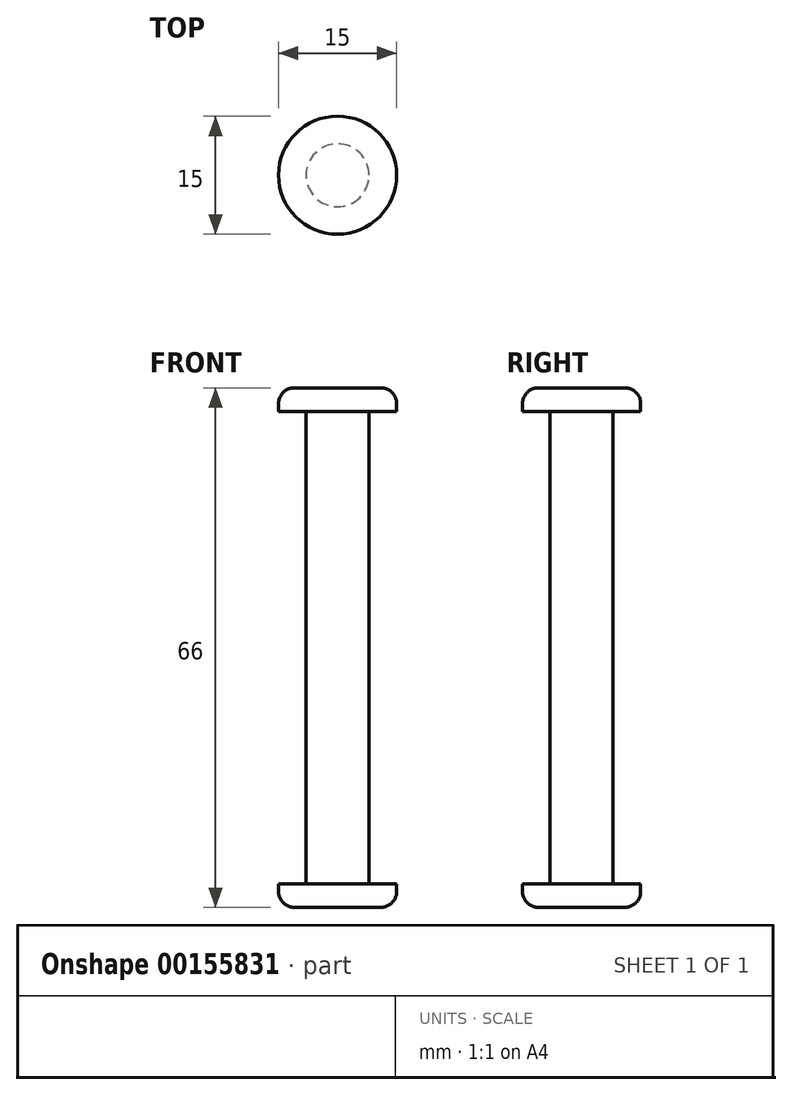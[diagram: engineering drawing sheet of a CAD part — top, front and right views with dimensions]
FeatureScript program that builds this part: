
annotation { "Feature Type Name" : "Feature", "Feature Type Description" : "" }
export const myFeature = defineFeature(function(context is Context, id is Id, definition is map)
    precondition{}
    {
        {
            var Q0;
            Q0=qCreatedBy(makeId("Top.planeOp"),FACE);
            var sketch = newSketch(context, id + "F0", { "sketchPlane" : qUnion([Q0])});
            skCircle(sketch, "E0", {"center": v(0, 0) * mm, "radius": 7.5 * mm});
            skSolve(sketch);
        }
        {
            var Q0;
            Q0 = qSketchRegion(id + "F0", true);
            extrude(context, id + "F1", {"entities" : qUnion([Q0]), "depth" : 3 * mm});
        }
        {
            var Q0;
            Q0=makeQuery(id+"F1.opExtrude","CAP_FACE",FACE,{"disambiguationData":[OSD([sQuery(id+"F0.wireOp",EDGE,"E0")])],"isStart":false});
            var sketch = newSketch(context, id + "F2", { "sketchPlane" : qUnion([Q0])});
            skCircle(sketch, "E1", {"center": v(0, 0) * mm, "radius": 4 * mm});
            skSolve(sketch);
        }
        {
            var Q0;
            Q0 = qSketchRegion(id + "F2", true);
            extrude(context, id + "F3", {"entities" : qUnion([Q0]), "operationType" : NewBodyOperationType.ADD, "depth" : 60 * mm});
        }
        {
            var Q0;
            Q0=makeQuery(id+"F3.opExtrude","CAP_FACE",FACE,{"disambiguationData":[OSD([sQuery(id+"F2.wireOp",EDGE,"E1")])],"isStart":false});
            var sketch = newSketch(context, id + "F4", { "sketchPlane" : qUnion([Q0])});
            skCircle(sketch, "E2", {"center": v(0, 0) * mm, "radius": 7.5 * mm});
            skSolve(sketch);
        }
        {
            var Q0;
            Q0 = qSketchRegion(id + "F4", true);
            extrude(context, id + "F5", {"entities" : qUnion([Q0]), "operationType" : NewBodyOperationType.ADD, "depth" : 3 * mm});
        }
        {
            var Q0;
            Q0=makeQuery(id+"F5.opExtrude","CAP_EDGE",EDGE,{"disambiguationData":[OSD([sQuery(id+"F4.wireOp",EDGE,"E2")])],"isStart":false});
            var Q1;
            Q1=makeQuery(id+"F1.opExtrude","CAP_EDGE",EDGE,{"disambiguationData":[OSD([sQuery(id+"F0.wireOp",EDGE,"E0")])],"isStart":true});
            fillet(context, id + "F6", {"entities" : qUnion([Q0, Q1]), "radius" : 2 * mm, "tangentPropagation" : true, "allowEdgeOverflow" : false});
        }
    });
